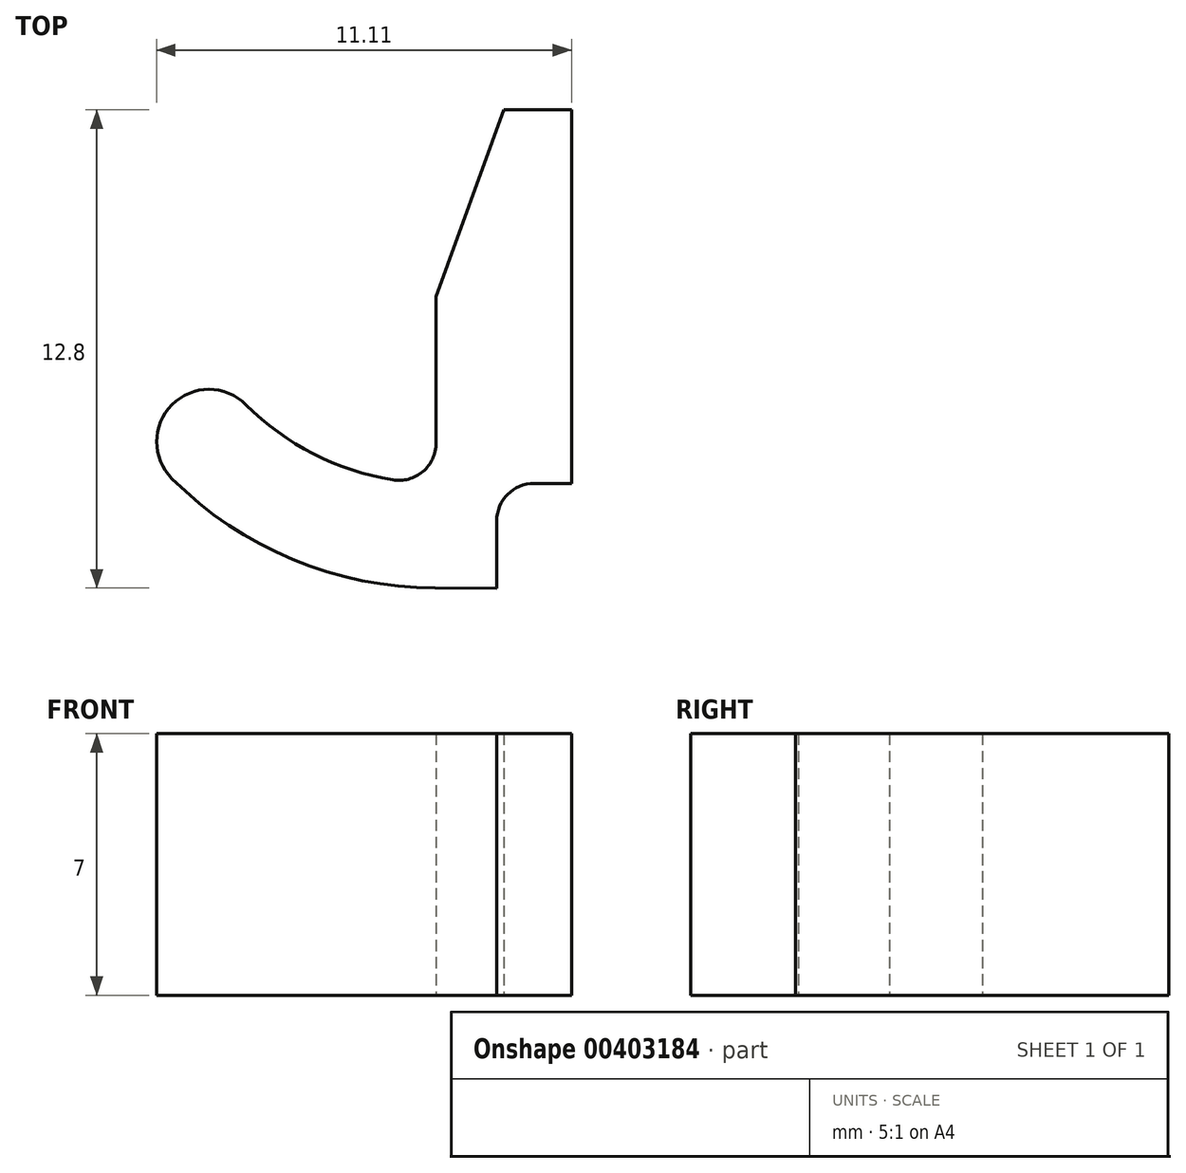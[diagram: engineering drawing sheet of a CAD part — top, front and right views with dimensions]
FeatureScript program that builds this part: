
annotation { "Feature Type Name" : "Feature", "Feature Type Description" : "" }
export const myFeature = defineFeature(function(context is Context, id is Id, definition is map)
    precondition{}
    {
        {
            var Q0;
            Q0=qCreatedBy(makeId("Top.planeOp"),FACE);
            var sketch = newSketch(context, id + "F0", { "sketchPlane" : qUnion([Q0])});
            skLineSegment(sketch, "E0", {"start": v(0, 0) * mm, "end": v(0, 6.77) * mm, "construction": true});
            skLineSegment(sketch, "E1", {"start": v(0, 6.77) * mm, "end": v(2, 6.77) * mm});
            skLineSegment(sketch, "E2", {"start": v(2, 6.77) * mm, "end": v(2, 16.77) * mm});
            skLineSegment(sketch, "E3", {"start": v(2, 16.77) * mm, "end": v(-1.62, 16.77) * mm});
            skLineSegment(sketch, "E4", {"start": v(-1.62, 16.77) * mm, "end": v(-1.62, 7.85) * mm});
            skLineSegment(sketch, "E5", {"start": v(0, 6.77) * mm, "end": v(-1.62, 6.77) * mm, "construction": true});
            skArc(sketch, "E6", {"start": v(-2.79, 6.87) * mm, "mid": v(-4.9, 7.56) * mm, "end": v(-6.72, 8.88) * mm});
            skArc(sketch, "E7.0", {"start": v(-1.65, 3.97) * mm, "mid": v(-5.46, 4.74) * mm, "end": v(-8.7, 6.9) * mm});
            skLineSegment(sketch, "E8", {"start": v(-6.72, 8.88) * mm, "end": v(-8.7, 6.9) * mm});
            skLineSegment(sketch, "E9", {"start": v(-1.62, 13.97) * mm, "end": v(-6.72, 8.88) * mm, "construction": true});
            skLineSegment(sketch, "E10", {"start": v(-1.65, 3.97) * mm, "end": v(0, 3.97) * mm});
            skLineSegment(sketch, "E11", {"start": v(0, 3.97) * mm, "end": v(0, 6.77) * mm});
            skLineSegment(sketch, "E12", {"start": v(0.19, 16.77) * mm, "end": v(-1.62, 11.77) * mm});
            skArc(sketch, "E13", {"start": v(-8.7, 6.9) * mm, "mid": v(-8.7, 8.88) * mm, "end": v(-6.72, 8.88) * mm});
            skPoint(sketch, "E14.visualSharp", {"position": v(-1.62, 6.77) * mm});
            skArc(sketch, "E14.filletArc", {"start": v(-2.79, 6.87) * mm, "mid": v(-1.98, 7.1) * mm, "end": v(-1.62, 7.85) * mm});
            skSolve(sketch);
        }
        {
            var Q0;
            Q0=makeQuery(id+"F0.imprint","IMPRINT",FACE,{"disambiguationData":[TD([[makeQuery(id+"F0.imprint","IMPRINT",EDGE,{"derivedFrom":sQuery(id+"F0.wireOp",EDGE,"E1")}),1.0]])]});
            var Q1;
            Q1=makeQuery(id+"F0.imprint","IMPRINT",FACE,{"disambiguationData":[TD([[makeQuery(id+"F0.imprint","IMPRINT",EDGE,{"derivedFrom":sQuery(id+"F0.wireOp",EDGE,"E8")}),-1.0]])]});
            extrude(context, id + "F1", {"entities" : qUnion([Q0, Q1]), "depth" : 7 * mm});
        }
        {
            var Q0;
            Q0=makeQuery(id+"F1.opExtrude","SWEPT_EDGE",EDGE,{"disambiguationData":[OSD([sQuery(id+"F0.wireOp",EDGE,"E1"),sQuery(id+"F0.wireOp",EDGE,"E11")])]});
            fillet(context, id + "F2", {"entities" : qUnion([Q0]), "radius" : 1 * mm, "tangentPropagation" : true, "allowEdgeOverflow" : false});
        }
    });
